# Revit family: F1V_2511-2543-2606_OS275
name_source: partatom
category: Finestre
units: mm (PartAtom-declared; Revit-internal decimal feet)

## family parameters
Condiviso = No
Host = Muro
Numero OmniClass = 23.30.20.00
Punto di calcolo locali = No
Sempre verticale = Sì
Taglio con vuoti quando caricato = No
Titolo OmniClass = Windows

## types (4) — shared parameters
Altezza di default del davanzale = 800 mm
Chiusura muro = Per host
Costruzione analitica = <Nessuno>
Descrizione = Finestra 1 anta e ribalta
H_Max = 1200 mm  [stored 3.93701 ft]
H_Min = 660 mm
L_Max = 1400 mm
L_Min = 560 mm
Maniglia_alta = 1050 mm  [stored 3.44488 ft]
Maniglia_media = 500 mm  [stored 1.64042 ft]
Modello = OS2 75
Produttore = Secco Sistemi Spa
URL = https://www.seccosistemi.com
WARNING = Sì
altezza maniglia = 500 mm  [stored 1.64042 ft]
n2_scarichi = 2
n3_scarichi = 3
numero_scarichi = 3

## per-type parameters (varying)
| type | Altezza | H | H1 | H_fermavetro | H_man | H_maniglia | H_vetro | L | L1 | L_fermavetro | L_vetro | Larghezza | MATERIALE | Maniglia_bassa |
| Ottone | 2000 mm  [stored 6.56168 ft] | 1200 mm  [stored 3.93701 ft] | 1200 mm  [stored 3.93701 ft] | 1136 mm  [stored 3.72703 ft] | 1050 mm  [stored 3.44488 ft] | 1050 mm  [stored 3.44488 ft] | 1124 mm  [stored 3.68766 ft] | 1000 mm  [stored 3.28084 ft] | 1000 mm  [stored 3.28084 ft] | 936 mm  [stored 3.07087 ft] | 924 mm  [stored 3.0315 ft] | 1000 mm  [stored 3.28084 ft] | Ottone | 600 mm |
| Acciaio inox | 500 mm  [stored 1.64042 ft] | 660 mm | 660 mm | 596 mm | 330 mm | 330 mm | 584 mm | 1400 mm | 1400 mm | 1336 mm | 1324 mm | 2000 mm  [stored 6.56168 ft] | Acciaio inox, spazzolato | 330 mm |
| Acciaio zincato | 2000 mm  [stored 6.56168 ft] | 1200 mm  [stored 3.93701 ft] | 1200 mm  [stored 3.93701 ft] | 1136 mm  [stored 3.72703 ft] | 1050 mm  [stored 3.44488 ft] | 1050 mm  [stored 3.44488 ft] | 1124 mm  [stored 3.68766 ft] | 1000 mm  [stored 3.28084 ft] | 1000 mm  [stored 3.28084 ft] | 936 mm  [stored 3.07087 ft] | 924 mm  [stored 3.0315 ft] | 1000 mm  [stored 3.28084 ft] | Acciaio zincato | 600 mm |
| Acciaio corten | 2000 mm  [stored 6.56168 ft] | 1200 mm  [stored 3.93701 ft] | 1200 mm  [stored 3.93701 ft] | 1136 mm  [stored 3.72703 ft] | 1050 mm  [stored 3.44488 ft] | 1050 mm  [stored 3.44488 ft] | 1124 mm  [stored 3.68766 ft] | 1000 mm  [stored 3.28084 ft] | 1000 mm  [stored 3.28084 ft] | 936 mm  [stored 3.07087 ft] | 924 mm  [stored 3.0315 ft] | 1000 mm  [stored 3.28084 ft] | Acciaio corten | 600 mm |

note: [stored X ft] marks values corroborated as IEEE doubles in the binary element streams (Revit-internal decimal feet)
